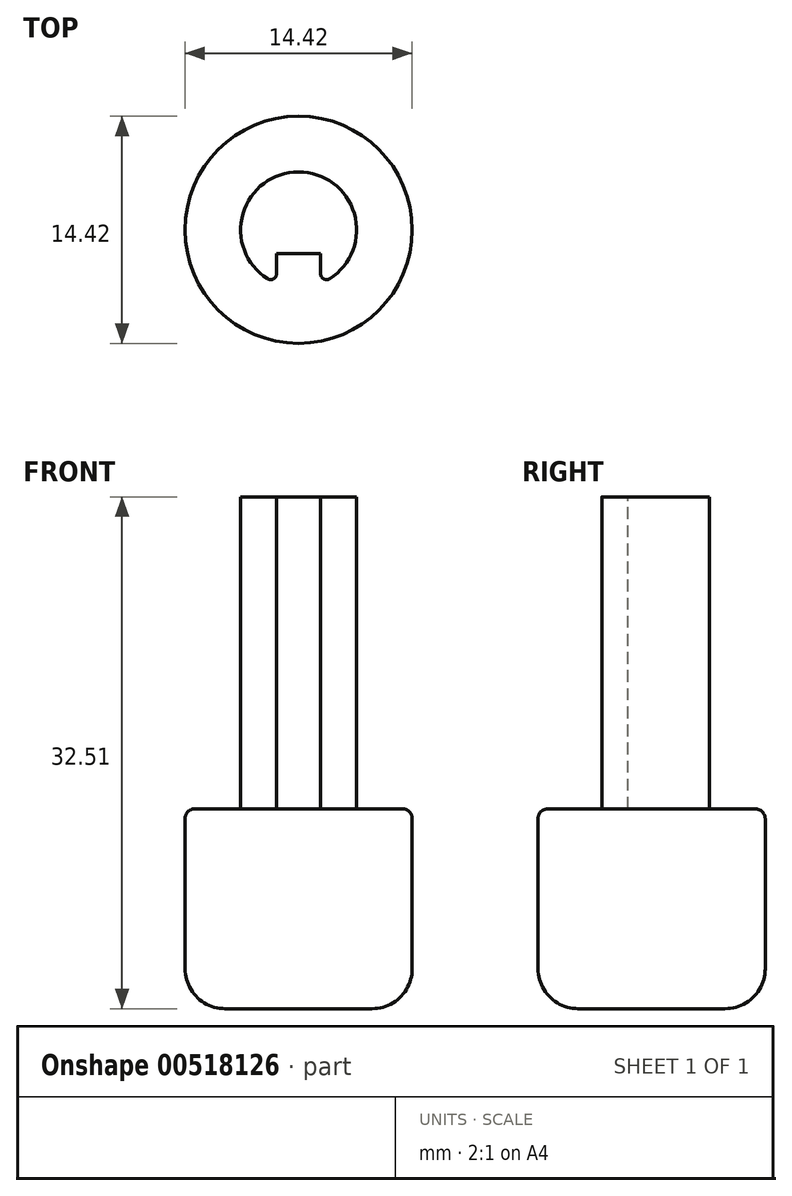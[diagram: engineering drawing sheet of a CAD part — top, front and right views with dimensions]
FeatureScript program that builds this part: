
annotation { "Feature Type Name" : "Feature", "Feature Type Description" : "" }
export const myFeature = defineFeature(function(context is Context, id is Id, definition is map)
    precondition{}
    {
        {
            var Q0;
            Q0=qCreatedBy(makeId("Top.planeOp"),FACE);
            var sketch = newSketch(context, id + "F0", { "sketchPlane" : qUnion([Q0])});
            skCircle(sketch, "E0", {"center": v(0, 0) * mm, "radius": 3.68 * mm});
            skSolve(sketch);
        }
        {
            var Q0;
            Q0 = qSketchRegion(id + "F0", true);
            extrude(context, id + "F1", {"entities" : qUnion([Q0]), "depth" : 19.8 * mm, "offsetDistance" : 25.4 * mm});
        }
        {
            var Q0;
            Q0=makeQuery(id+"F1.opExtrude","CAP_FACE",FACE,{"disambiguationData":[OSD([sQuery(id+"F0.wireOp",EDGE,"E0")])],"isStart":false});
            var sketch = newSketch(context, id + "F2", { "sketchPlane" : qUnion([Q0])});
            skLineSegment(sketch, "E1.bottom", {"start": v(-1.4, -3.68) * mm, "end": v(1.4, -3.68) * mm});
            skLineSegment(sketch, "E1.top", {"start": v(-1.4, -1.51) * mm, "end": v(1.4, -1.51) * mm});
            skLineSegment(sketch, "E1.left", {"start": v(-1.4, -3.68) * mm, "end": v(-1.4, -1.51) * mm});
            skLineSegment(sketch, "E1.right", {"start": v(1.4, -3.68) * mm, "end": v(1.4, -1.51) * mm});
            skSolve(sketch);
        }
        {
            var Q0;
            Q0 = qSketchRegion(id + "F2", true);
            extrude(context, id + "F3", {"entities" : qUnion([Q0]), "operationType" : NewBodyOperationType.REMOVE, "oppositeDirection" : true, "depth" : 25.4 * mm, "offsetDistance" : 25.4 * mm});
        }
        {
            var Q0;
            Q0=makeQuery(id+"F3.boolean.opBoolean","INTERSECT",EDGE,{"derivedFrom":[makeQuery(id+"F1.opExtrude","SWEPT_FACE",FACE,{"disambiguationData":[OSD([sQuery(id+"F0.wireOp",EDGE,"E0")])]}),makeQuery(id+"F3.opExtrude","SWEPT_FACE",FACE,{"disambiguationData":[OSD([sQuery(id+"F2.wireOp",EDGE,"E1.right")])]})]});
            var Q1;
            Q1=makeQuery(id+"F3.boolean.opBoolean","INTERSECT",EDGE,{"derivedFrom":[makeQuery(id+"F1.opExtrude","SWEPT_FACE",FACE,{"disambiguationData":[OSD([sQuery(id+"F0.wireOp",EDGE,"E0")])]}),makeQuery(id+"F3.opExtrude","SWEPT_FACE",FACE,{"disambiguationData":[OSD([sQuery(id+"F2.wireOp",EDGE,"E1.left")])]})]});
            fillet(context, id + "F4", {"entities" : qUnion([Q0, Q1]), "radius" : 0.38 * mm, "tangentPropagation" : true, "allowEdgeOverflow" : false});
        }
        {
            var Q0;
            Q0=makeQuery(id+"F1.opExtrude","CAP_FACE",FACE,{"disambiguationData":[OSD([sQuery(id+"F0.wireOp",EDGE,"E0")])],"isStart":true});
            var sketch = newSketch(context, id + "F5", { "sketchPlane" : qUnion([Q0])});
            skCircle(sketch, "E2", {"center": v(0, 0) * mm, "radius": 7.21 * mm});
            skSolve(sketch);
        }
        {
            var Q0;
            Q0 = qSketchRegion(id + "F5", true);
            extrude(context, id + "F6", {"entities" : qUnion([Q0]), "operationType" : NewBodyOperationType.ADD, "depth" : 12.7 * mm, "offsetDistance" : 25.4 * mm});
        }
        {
            var Q0;
            Q0=makeQuery(id+"F6.opExtrude","CAP_EDGE",EDGE,{"disambiguationData":[OSD([sQuery(id+"F5.wireOp",EDGE,"E2")])],"isStart":false});
            fillet(context, id + "F7", {"entities" : qUnion([Q0]), "radius" : 2.54 * mm, "tangentPropagation" : true, "allowEdgeOverflow" : false});
        }
        {
            var Q0;
            Q0=makeQuery(id+"F6.opExtrude","CAP_EDGE",EDGE,{"disambiguationData":[OSD([sQuery(id+"F5.wireOp",EDGE,"E2")])],"isStart":true});
            fillet(context, id + "F8", {"entities" : qUnion([Q0]), "radius" : 0.64 * mm, "tangentPropagation" : true, "allowEdgeOverflow" : false});
        }
    });
